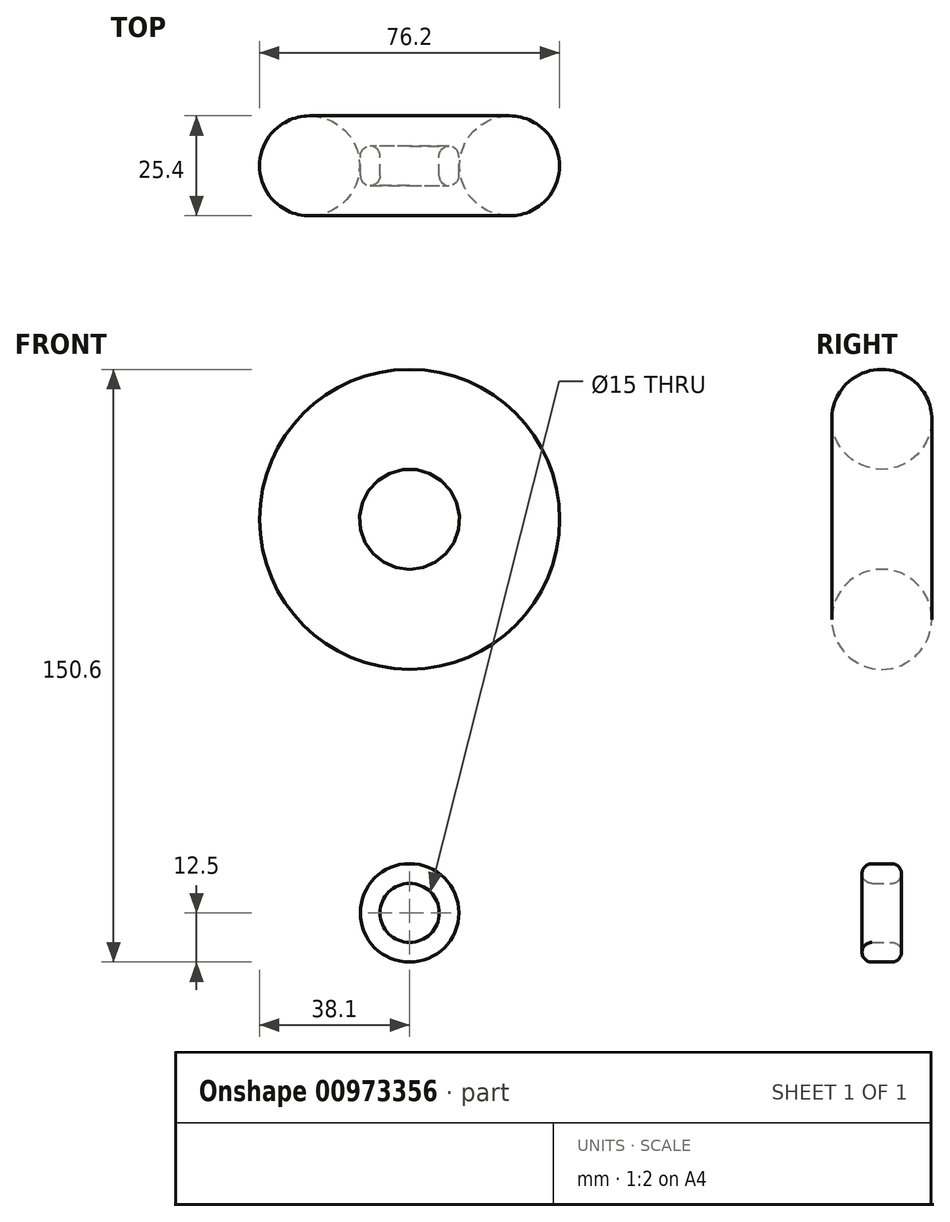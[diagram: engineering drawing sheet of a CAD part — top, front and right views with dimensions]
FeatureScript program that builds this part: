
annotation { "Feature Type Name" : "Feature", "Feature Type Description" : "" }
export const myFeature = defineFeature(function(context is Context, id is Id, definition is map)
    precondition{}
    {
        {
            var Q0;
            Q0=qCreatedBy(makeId("Top.planeOp"),FACE);
            var sketch = newSketch(context, id + "F0", { "sketchPlane" : qUnion([Q0])});
            skLineSegment(sketch, "E0", {"start": v(0, -10) * mm, "end": v(0, 10) * mm});
            skLineSegment(sketch, "E1", {"start": v(0, 0) * mm, "end": v(25.4, 0) * mm});
            skCircle(sketch, "E2", {"center": v(25.4, 0) * mm, "radius": 12.7 * mm});
            skSolve(sketch);
        }
        {
            var Q0;
            Q0=makeQuery(id+"F0.imprint","IMPRINT",FACE,{"disambiguationData":[TD([[makeQuery(id+"F0.imprint","IMPRINT",EDGE,{"derivedFrom":sQuery(id+"F0.wireOp",EDGE,"E2")}),1.0]])]});
            var Q1;
            Q1=sQuery(id+"F0.wireOp",EDGE,"E0");
            revolve(context, id + "F1", {"surfaceOperationType" : NewSurfaceOperationType.NEW, "entities" : qUnion([Q0]), "axis" : qUnion([Q1]), "revolveType" : RevolveType.FULL});
        }
        {
            var Q0;
            Q0=makeQuery(id+"F1.opRevolve","SWEPT_BODY",BODY,{"disambiguationData":[OSD([sQuery(id+"F0.wireOp",EDGE,"E2")])]});
            transform(context, id + "F2", {"entities" : qUnion([Q0]), "transformType" : TransformType.TRANSLATION_3D, "dx" : 0 * mm, "dy" : 0 * mm, "dz" : 100 * mm, "makeCopy" : false});
        }
        {
            var Q0;
            Q0=qCreatedBy(makeId("Front.planeOp"),FACE);
            var sketch = newSketch(context, id + "F3", { "sketchPlane" : qUnion([Q0])});
            skCircle(sketch, "E3", {"center": v(0, 0) * mm, "radius": 7.5 * mm});
            skCircle(sketch, "E4.0", {"center": v(0, 0) * mm, "radius": 12.5 * mm});
            skSolve(sketch);
        }
        {
            var Q0;
            Q0 = qSketchRegion(id + "F3", true);
            extrude(context, id + "F4", {"entities" : qUnion([Q0]), "depth" : 10 * mm, "offsetDistance" : 25 * mm, "symmetric" : true});
        }
        {
            var Q0;
            Q0=makeQuery(id+"F4.opExtrude","CAP_EDGE",EDGE,{"disambiguationData":[OSD([sQuery(id+"F3.wireOp",EDGE,"E4.0")])],"isStart":false});
            var Q1;
            Q1=makeQuery(id+"F4.opExtrude","CAP_EDGE",EDGE,{"disambiguationData":[OSD([sQuery(id+"F3.wireOp",EDGE,"E4.0")])],"isStart":true});
            var Q2;
            Q2=makeQuery(id+"F4.opExtrude","CAP_EDGE",EDGE,{"disambiguationData":[OSD([sQuery(id+"F3.wireOp",EDGE,"E3")])],"isStart":false});
            var Q3;
            Q3=makeQuery(id+"F4.opExtrude","CAP_EDGE",EDGE,{"disambiguationData":[OSD([sQuery(id+"F3.wireOp",EDGE,"E3")])],"isStart":true});
            fillet(context, id + "F5", {"entities" : qUnion([Q0, Q1, Q2, Q3]), "tangentPropagation" : true, "radius" : 2.5 * mm, "defaultsChanged" : true, "vertexSettings" : [], "allowEdgeOverflow" : false});
        }
    });
